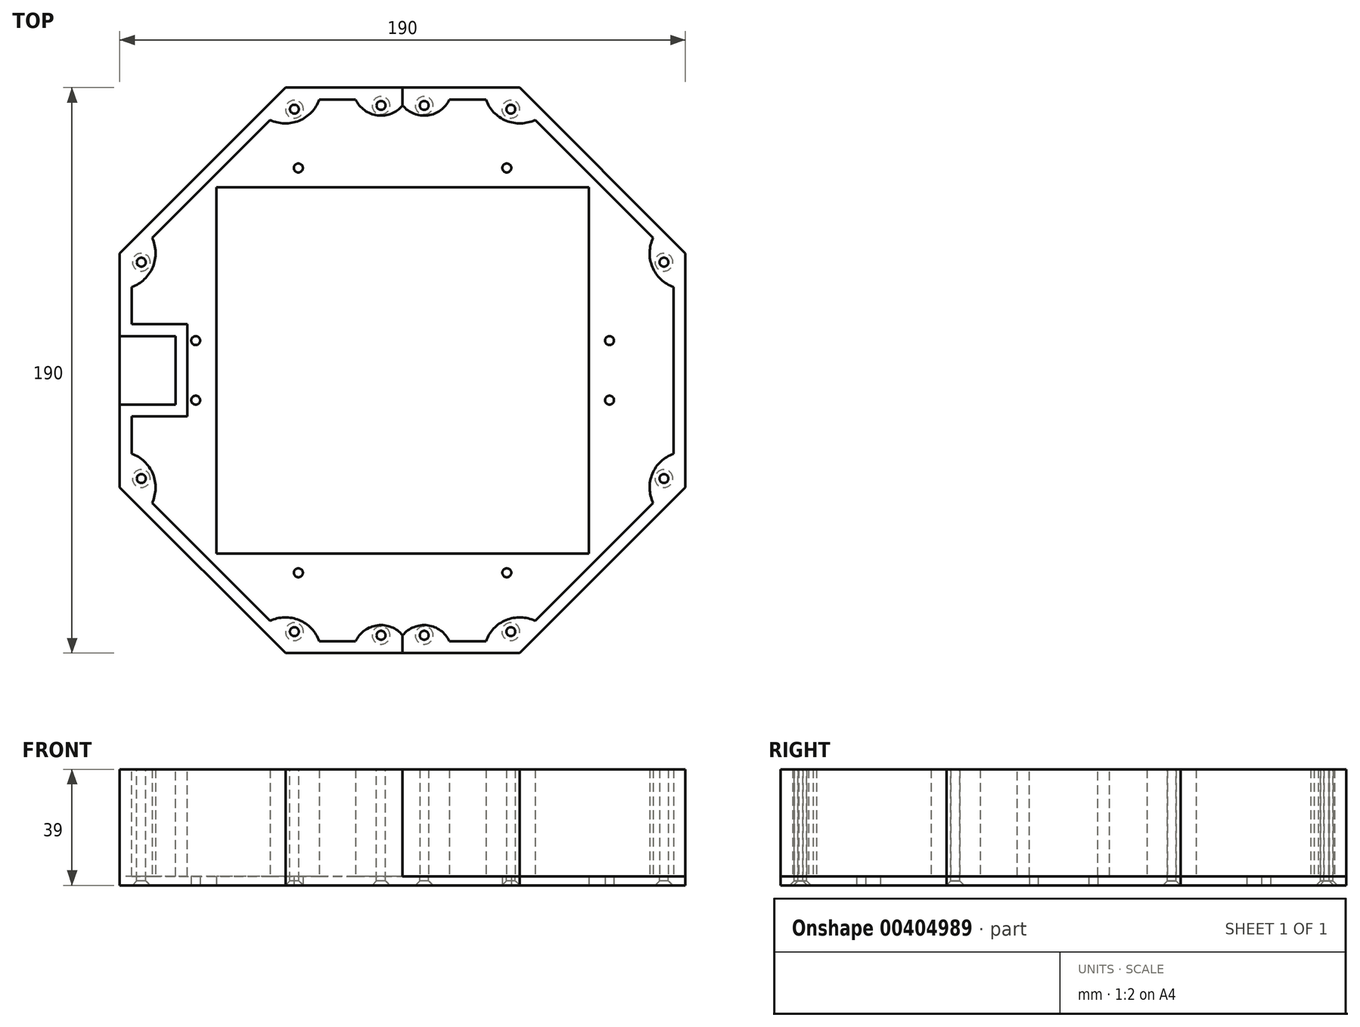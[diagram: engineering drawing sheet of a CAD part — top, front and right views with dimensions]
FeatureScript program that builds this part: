
annotation { "Feature Type Name" : "Feature", "Feature Type Description" : "" }
export const myFeature = defineFeature(function(context is Context, id is Id, definition is map)
    precondition{}
    {
        {
            var Q0;
            Q0=qCreatedBy(makeId("Top.planeOp"),FACE);
            var sketch = newSketch(context, id + "F0", { "sketchPlane" : qUnion([Q0])});
            skCircle(sketch, "E0.cCircle", {"center": v(0, 0) * mm, "radius": 95 * mm, "construction": true});
            skLineSegment(sketch, "E0.0", {"start": v(-95, -39.35) * mm, "end": v(-95, 39.35) * mm});
            skLineSegment(sketch, "E0.1", {"start": v(-95, 39.35) * mm, "end": v(-39.35, 95) * mm});
            skLineSegment(sketch, "E0.2", {"start": v(-39.35, 95) * mm, "end": v(39.35, 95) * mm});
            skLineSegment(sketch, "E0.3", {"start": v(39.35, 95) * mm, "end": v(95, 39.35) * mm});
            skLineSegment(sketch, "E0.4", {"start": v(95, 39.35) * mm, "end": v(95, -39.35) * mm});
            skLineSegment(sketch, "E0.5", {"start": v(95, -39.35) * mm, "end": v(39.35, -95) * mm});
            skLineSegment(sketch, "E0.6", {"start": v(39.35, -95) * mm, "end": v(-39.35, -95) * mm});
            skLineSegment(sketch, "E0.7", {"start": v(-39.35, -95) * mm, "end": v(-95, -39.35) * mm});
            skPoint(sketch, "E0.0.midPoint", {"position": v(-95, 0) * mm});
            skLineSegment(sketch, "E1.0", {"start": v(-91, -37.7) * mm, "end": v(-91, 37.7) * mm});
            skLineSegment(sketch, "E1.1", {"start": v(-37.7, -91) * mm, "end": v(-91, -37.7) * mm});
            skLineSegment(sketch, "E1.2", {"start": v(-91, 37.7) * mm, "end": v(-37.7, 91) * mm});
            skLineSegment(sketch, "E1.3", {"start": v(37.7, -91) * mm, "end": v(-37.7, -91) * mm});
            skLineSegment(sketch, "E1.4", {"start": v(-37.7, 91) * mm, "end": v(37.7, 91) * mm});
            skLineSegment(sketch, "E1.5", {"start": v(37.7, 91) * mm, "end": v(91, 37.7) * mm});
            skLineSegment(sketch, "E1.6", {"start": v(91, 37.7) * mm, "end": v(91, -37.7) * mm});
            skLineSegment(sketch, "E1.7", {"start": v(91, -37.7) * mm, "end": v(37.7, -91) * mm});
            skLineSegment(sketch, "E2", {"start": v(0, 91) * mm, "end": v(0, 95) * mm});
            skLineSegment(sketch, "E3", {"start": v(-95, 0) * mm, "end": v(95, 0) * mm});
            skLineSegment(sketch, "E4", {"start": v(0, -91) * mm, "end": v(0, -95) * mm});
            skCircle(sketch, "E5", {"center": v(-87.77, 36.36) * mm, "radius": 1.5 * mm});
            skCircle(sketch, "E6", {"center": v(-7.25, 89) * mm, "radius": 1.5 * mm});
            skCircle(sketch, "E7", {"center": v(7.25, 89) * mm, "radius": 1.5 * mm});
            skLineSegment(sketch, "E8", {"start": v(0, 0) * mm, "end": v(-95, 39.35) * mm, "construction": true});
            skLineSegment(sketch, "E9", {"start": v(0, 0) * mm, "end": v(0, 89) * mm, "construction": true});
            skLineSegment(sketch, "E10", {"start": v(-7.25, 89) * mm, "end": v(0, 89) * mm, "construction": true});
            skLineSegment(sketch, "E11", {"start": v(7.25, 89) * mm, "end": v(0, 89) * mm, "construction": true});
            skArc(sketch, "E12", {"start": v(-15.77, 91) * mm, "mid": v(-7.25, 85.59) * mm, "end": v(1.27, 91) * mm});
            skArc(sketch, "E13", {"start": v(-1.27, 91) * mm, "mid": v(7.25, 85.59) * mm, "end": v(15.77, 91) * mm});
            skLineSegment(sketch, "E14", {"start": v(0, 89) * mm, "end": v(0, 91) * mm});
            skArc(sketch, "E15.1.0", {"start": v(15.77, -91) * mm, "mid": v(7.25, -85.59) * mm, "end": v(-1.27, -91) * mm});
            skCircle(sketch, "E15.1.1", {"center": v(7.25, -89) * mm, "radius": 1.5 * mm});
            skArc(sketch, "E15.1.2", {"start": v(1.27, -91) * mm, "mid": v(-7.25, -85.59) * mm, "end": v(-15.77, -91) * mm});
            skCircle(sketch, "E15.1.3", {"center": v(-7.25, -89) * mm, "radius": 1.5 * mm});
            skLineSegment(sketch, "E15.1.4", {"start": v(0, -89) * mm, "end": v(0, -91) * mm});
            skArc(sketch, "E16.trimOffspring", {"start": v(-91, 28) * mm, "mid": v(-83.89, 34.75) * mm, "end": v(-84.15, 44.54) * mm});
            skCircle(sketch, "E17.1.0", {"center": v(-87.77, -36.35) * mm, "radius": 1.5 * mm});
            skArc(sketch, "E17.1.1", {"start": v(-84.15, -44.54) * mm, "mid": v(-83.89, -34.75) * mm, "end": v(-91, -28) * mm});
            skCircle(sketch, "E17.2.0", {"center": v(-36.36, -87.77) * mm, "radius": 1.5 * mm});
            skArc(sketch, "E17.2.1", {"start": v(-28, -91) * mm, "mid": v(-34.75, -83.89) * mm, "end": v(-44.54, -84.15) * mm});
            skCircle(sketch, "E17.3.0", {"center": v(36.36, -87.77) * mm, "radius": 1.5 * mm});
            skArc(sketch, "E17.3.1", {"start": v(44.54, -84.15) * mm, "mid": v(34.75, -83.89) * mm, "end": v(28, -91) * mm});
            skCircle(sketch, "E17.4.0", {"center": v(87.77, -36.36) * mm, "radius": 1.5 * mm});
            skArc(sketch, "E17.4.1", {"start": v(91, -28) * mm, "mid": v(83.89, -34.75) * mm, "end": v(84.15, -44.54) * mm});
            skCircle(sketch, "E17.5.0", {"center": v(87.77, 36.35) * mm, "radius": 1.5 * mm});
            skArc(sketch, "E17.5.1", {"start": v(84.15, 44.54) * mm, "mid": v(83.89, 34.75) * mm, "end": v(91, 28) * mm});
            skCircle(sketch, "E17.6.0", {"center": v(36.36, 87.77) * mm, "radius": 1.5 * mm});
            skArc(sketch, "E17.6.1", {"start": v(28, 91) * mm, "mid": v(34.75, 83.89) * mm, "end": v(44.54, 84.15) * mm});
            skCircle(sketch, "E17.7.0", {"center": v(-36.35, 87.77) * mm, "radius": 1.5 * mm});
            skArc(sketch, "E17.7.1", {"start": v(-44.54, 84.15) * mm, "mid": v(-34.75, 83.89) * mm, "end": v(-28, 91) * mm});
            skSolve(sketch);
        }
        {
            var Q0;
            Q0=makeQuery(id+"F0.imprint","IMPRINT",FACE,{"disambiguationData":[TD([[makeQuery(id+"F0.imprint","IMPRINT",EDGE,{"derivedFrom":sQuery(id+"F0.wireOp",EDGE,"E6")}),-1.0]])]});
            var Q1;
            Q1=makeQuery(id+"F0.imprint","IMPRINT",FACE,{"disambiguationData":[TD([[makeQuery(id+"F0.imprint","IMPRINT",EDGE,{"derivedFrom":sQuery(id+"F0.wireOp",EDGE,"E7")}),-1.0]])]});
            var Q2;
            {var subQ0=sQuery(id+"F0.wireOp",EDGE,"E14");Q2=makeQuery(id+"F0.imprint","IMPRINT",FACE,{"disambiguationData":[TD([[makeQuery(id+"F0.imprint","IMPRINT",EDGE,{"derivedFrom":subQ0}),-1.0]])]});}
            var Q3;
            {var subQ0=sQuery(id+"F0.wireOp",EDGE,"E14");Q3=makeQuery(id+"F0.imprint","IMPRINT",FACE,{"disambiguationData":[TD([[makeQuery(id+"F0.imprint","IMPRINT",EDGE,{"derivedFrom":subQ0}),1.0]])]});}
            var Q4;
            {var subQ11=sQuery(id+"F0.wireOp",EDGE,"E1.2");Q4=makeQuery(id+"F0.imprint","IMPRINT",FACE,{"disambiguationData":[TD([[makeQuery(id+"F0.imprint","IMPRINT",EDGE,{"derivedFrom":subQ11}),-1.0]])]});}
            var Q5;
            {var subQ8=sQuery(id+"F0.wireOp",EDGE,"E0.1");Q5=makeQuery(id+"F0.imprint","IMPRINT",FACE,{"disambiguationData":[TD([[makeQuery(id+"F0.imprint","IMPRINT",EDGE,{"derivedFrom":subQ8}),-1.0]])]});}
            var Q6;
            {var subQ4=sQuery(id+"F0.wireOp",EDGE,"E0.3");Q6=makeQuery(id+"F0.imprint","IMPRINT",FACE,{"disambiguationData":[TD([[makeQuery(id+"F0.imprint","IMPRINT",EDGE,{"derivedFrom":subQ4}),-1.0]])]});}
            var Q7;
            Q7=makeQuery(id+"F0.imprint","IMPRINT",FACE,{"disambiguationData":[TD([[makeQuery(id+"F0.imprint","IMPRINT",EDGE,{"derivedFrom":sQuery(id+"F0.wireOp",EDGE,"E17.5.0")}),-1.0]])]});
            var Q8;
            Q8=makeQuery(id+"F0.imprint","IMPRINT",FACE,{"disambiguationData":[TD([[makeQuery(id+"F0.imprint","IMPRINT",EDGE,{"derivedFrom":sQuery(id+"F0.wireOp",EDGE,"E17.6.0")}),-1.0]])]});
            var Q9;
            {var subQ15=sQuery(id+"F0.wireOp",EDGE,"E16.trimOffspring");Q9=makeQuery(id+"F0.imprint","IMPRINT",FACE,{"disambiguationData":[TD([[makeQuery(id+"F0.imprint","IMPRINT",EDGE,{"derivedFrom":subQ15}),-1.0]])]});}
            extrude(context, id + "F1", {"entities" : qUnion([Q0, Q1, Q2, Q3, Q4, Q5, Q6, Q7, Q8, Q9]), "oppositeDirection" : true, "depth" : 3 * mm});
        }
        {
            var Q0;
            Q0=makeQuery(id+"F0.imprint","IMPRINT",FACE,{"disambiguationData":[TD([[makeQuery(id+"F0.imprint","IMPRINT",EDGE,{"derivedFrom":sQuery(id+"F0.wireOp",EDGE,"E17.1.0")}),-1.0]])]});
            var Q1;
            Q1=makeQuery(id+"F0.imprint","IMPRINT",FACE,{"disambiguationData":[TD([[makeQuery(id+"F0.imprint","IMPRINT",EDGE,{"derivedFrom":sQuery(id+"F0.wireOp",EDGE,"E17.4.0")}),-1.0]])]});
            var Q2;
            Q2=makeQuery(id+"F0.imprint","IMPRINT",FACE,{"disambiguationData":[TD([[makeQuery(id+"F0.imprint","IMPRINT",EDGE,{"derivedFrom":sQuery(id+"F0.wireOp",EDGE,"E17.3.0")}),-1.0]])]});
            var Q3;
            Q3=makeQuery(id+"F0.imprint","IMPRINT",FACE,{"disambiguationData":[TD([[makeQuery(id+"F0.imprint","IMPRINT",EDGE,{"derivedFrom":sQuery(id+"F0.wireOp",EDGE,"E15.1.1")}),-1.0]])]});
            var Q4;
            Q4=makeQuery(id+"F0.imprint","IMPRINT",FACE,{"disambiguationData":[TD([[makeQuery(id+"F0.imprint","IMPRINT",EDGE,{"derivedFrom":sQuery(id+"F0.wireOp",EDGE,"E15.1.3")}),-1.0]])]});
            var Q5;
            Q5=makeQuery(id+"F0.imprint","IMPRINT",FACE,{"disambiguationData":[TD([[makeQuery(id+"F0.imprint","IMPRINT",EDGE,{"derivedFrom":sQuery(id+"F0.wireOp",EDGE,"E17.2.0")}),-1.0]])]});
            var Q6;
            {var subQ2=sQuery(id+"F0.wireOp",EDGE,"E15.1.4");Q6=makeQuery(id+"F0.imprint","IMPRINT",FACE,{"disambiguationData":[TD([[makeQuery(id+"F0.imprint","IMPRINT",EDGE,{"derivedFrom":subQ2}),-1.0]])]});}
            var Q7;
            {var subQ3=sQuery(id+"F0.wireOp",EDGE,"E15.1.4");Q7=makeQuery(id+"F0.imprint","IMPRINT",FACE,{"disambiguationData":[TD([[makeQuery(id+"F0.imprint","IMPRINT",EDGE,{"derivedFrom":subQ3}),1.0]])]});}
            var Q8;
            {var subQ0=sQuery(id+"F0.wireOp",EDGE,"E17.1.1");Q8=makeQuery(id+"F0.imprint","IMPRINT",FACE,{"disambiguationData":[TD([[makeQuery(id+"F0.imprint","IMPRINT",EDGE,{"derivedFrom":subQ0}),-1.0]])]});}
            var Q9;
            {var subQ16=sQuery(id+"F0.wireOp",EDGE,"E0.5");Q9=makeQuery(id+"F0.imprint","IMPRINT",FACE,{"disambiguationData":[TD([[makeQuery(id+"F0.imprint","IMPRINT",EDGE,{"derivedFrom":subQ16}),-1.0]])]});}
            var Q10;
            {var subQ9=sQuery(id+"F0.wireOp",EDGE,"E0.7");Q10=makeQuery(id+"F0.imprint","IMPRINT",FACE,{"disambiguationData":[TD([[makeQuery(id+"F0.imprint","IMPRINT",EDGE,{"derivedFrom":subQ9}),-1.0]])]});}
            extrude(context, id + "F2", {"entities" : qUnion([Q0, Q1, Q2, Q3, Q4, Q5, Q6, Q7, Q8, Q9, Q10]), "oppositeDirection" : true, "depth" : 3 * mm});
        }
        {
            var Q0;
            {var subQ16=sQuery(id+"F0.wireOp",EDGE,"E0.5");Q0=makeQuery(id+"F0.imprint","IMPRINT",FACE,{"disambiguationData":[TD([[makeQuery(id+"F0.imprint","IMPRINT",EDGE,{"derivedFrom":subQ16}),-1.0]])]});}
            var Q1;
            {var subQ9=sQuery(id+"F0.wireOp",EDGE,"E0.3");Q1=makeQuery(id+"F0.imprint","IMPRINT",FACE,{"disambiguationData":[TD([[makeQuery(id+"F0.imprint","IMPRINT",EDGE,{"derivedFrom":subQ9}),-1.0]])]});}
            var Q2;
            Q2=makeQuery(id+"F0.imprint","IMPRINT",FACE,{"disambiguationData":[TD([[makeQuery(id+"F0.imprint","IMPRINT",EDGE,{"derivedFrom":sQuery(id+"F0.wireOp",EDGE,"E7")}),-1.0]])]});
            var Q3;
            Q3=makeQuery(id+"F0.imprint","IMPRINT",FACE,{"disambiguationData":[TD([[makeQuery(id+"F0.imprint","IMPRINT",EDGE,{"derivedFrom":sQuery(id+"F0.wireOp",EDGE,"E17.6.0")}),-1.0]])]});
            var Q4;
            Q4=makeQuery(id+"F0.imprint","IMPRINT",FACE,{"disambiguationData":[TD([[makeQuery(id+"F0.imprint","IMPRINT",EDGE,{"derivedFrom":sQuery(id+"F0.wireOp",EDGE,"E17.5.0")}),-1.0]])]});
            var Q5;
            Q5=makeQuery(id+"F0.imprint","IMPRINT",FACE,{"disambiguationData":[TD([[makeQuery(id+"F0.imprint","IMPRINT",EDGE,{"derivedFrom":sQuery(id+"F0.wireOp",EDGE,"E17.4.0")}),-1.0]])]});
            var Q6;
            Q6=makeQuery(id+"F0.imprint","IMPRINT",FACE,{"disambiguationData":[TD([[makeQuery(id+"F0.imprint","IMPRINT",EDGE,{"derivedFrom":sQuery(id+"F0.wireOp",EDGE,"E17.3.0")}),-1.0]])]});
            var Q7;
            Q7=makeQuery(id+"F0.imprint","IMPRINT",FACE,{"disambiguationData":[TD([[makeQuery(id+"F0.imprint","IMPRINT",EDGE,{"derivedFrom":sQuery(id+"F0.wireOp",EDGE,"E15.1.1")}),-1.0]])]});
            var Q8;
            {var subQ0=sQuery(id+"F0.wireOp",EDGE,"E14");Q8=makeQuery(id+"F0.imprint","IMPRINT",FACE,{"disambiguationData":[TD([[makeQuery(id+"F0.imprint","IMPRINT",EDGE,{"derivedFrom":subQ0}),-1.0]])]});}
            var Q9;
            {var subQ3=sQuery(id+"F0.wireOp",EDGE,"E15.1.4");Q9=makeQuery(id+"F0.imprint","IMPRINT",FACE,{"disambiguationData":[TD([[makeQuery(id+"F0.imprint","IMPRINT",EDGE,{"derivedFrom":subQ3}),1.0]])]});}
            extrude(context, id + "F3", {"entities" : qUnion([Q0, Q1, Q2, Q3, Q4, Q5, Q6, Q7, Q8, Q9]), "depth" : 36 * mm});
        }
        {
            var Q0;
            {var subQ2=sQuery(id+"F0.wireOp",EDGE,"E15.1.4");Q0=makeQuery(id+"F0.imprint","IMPRINT",FACE,{"disambiguationData":[TD([[makeQuery(id+"F0.imprint","IMPRINT",EDGE,{"derivedFrom":subQ2}),-1.0]])]});}
            var Q1;
            Q1=makeQuery(id+"F0.imprint","IMPRINT",FACE,{"disambiguationData":[TD([[makeQuery(id+"F0.imprint","IMPRINT",EDGE,{"derivedFrom":sQuery(id+"F0.wireOp",EDGE,"E15.1.3")}),-1.0]])]});
            var Q2;
            Q2=makeQuery(id+"F0.imprint","IMPRINT",FACE,{"disambiguationData":[TD([[makeQuery(id+"F0.imprint","IMPRINT",EDGE,{"derivedFrom":sQuery(id+"F0.wireOp",EDGE,"E17.2.0")}),-1.0]])]});
            var Q3;
            {var subQ9=sQuery(id+"F0.wireOp",EDGE,"E0.7");Q3=makeQuery(id+"F0.imprint","IMPRINT",FACE,{"disambiguationData":[TD([[makeQuery(id+"F0.imprint","IMPRINT",EDGE,{"derivedFrom":subQ9}),-1.0]])]});}
            var Q4;
            Q4=makeQuery(id+"F0.imprint","IMPRINT",FACE,{"disambiguationData":[TD([[makeQuery(id+"F0.imprint","IMPRINT",EDGE,{"derivedFrom":sQuery(id+"F0.wireOp",EDGE,"E17.1.0")}),-1.0]])]});
            var Q5;
            {var subQ14=sQuery(id+"F0.wireOp",EDGE,"E0.1");Q5=makeQuery(id+"F0.imprint","IMPRINT",FACE,{"disambiguationData":[TD([[makeQuery(id+"F0.imprint","IMPRINT",EDGE,{"derivedFrom":subQ14}),-1.0]])]});}
            var Q6;
            Q6=makeQuery(id+"F0.imprint","IMPRINT",FACE,{"disambiguationData":[TD([[makeQuery(id+"F0.imprint","IMPRINT",EDGE,{"derivedFrom":sQuery(id+"F0.wireOp",EDGE,"E5")}),-1.0]])]});
            var Q7;
            Q7=makeQuery(id+"F0.imprint","IMPRINT",FACE,{"disambiguationData":[TD([[makeQuery(id+"F0.imprint","IMPRINT",EDGE,{"derivedFrom":sQuery(id+"F0.wireOp",EDGE,"E17.7.0")}),-1.0]])]});
            var Q8;
            Q8=makeQuery(id+"F0.imprint","IMPRINT",FACE,{"disambiguationData":[TD([[makeQuery(id+"F0.imprint","IMPRINT",EDGE,{"derivedFrom":sQuery(id+"F0.wireOp",EDGE,"E6")}),-1.0]])]});
            var Q9;
            {var subQ0=sQuery(id+"F0.wireOp",EDGE,"E14");Q9=makeQuery(id+"F0.imprint","IMPRINT",FACE,{"disambiguationData":[TD([[makeQuery(id+"F0.imprint","IMPRINT",EDGE,{"derivedFrom":subQ0}),1.0]])]});}
            extrude(context, id + "F4", {"entities" : qUnion([Q0, Q1, Q2, Q3, Q4, Q5, Q6, Q7, Q8, Q9]), "depth" : 36 * mm});
        }
        {
            var Q0;
            Q0=makeQuery(id+"F2.opExtrude","CAP_FACE",FACE,{"disambiguationData":[OSD([sQuery(id+"F0.wireOp",EDGE,"E0.0"),sQuery(id+"F0.wireOp",EDGE,"E0.1"),sQuery(id+"F0.wireOp",EDGE,"E0.2"),sQuery(id+"F0.wireOp",EDGE,"E0.3"),sQuery(id+"F0.wireOp",EDGE,"E0.4"),sQuery(id+"F0.wireOp",EDGE,"E3")])],"isStart":false});
            var sketch = newSketch(context, id + "F5", { "sketchPlane" : qUnion([Q0])});
            skLineSegment(sketch, "E18", {"start": v(0, 0) * mm, "end": v(-74, 0) * mm, "construction": true});
            skLineSegment(sketch, "E19", {"start": v(0, 0) * mm, "end": v(74, 0) * mm, "construction": true});
            skLineSegment(sketch, "E20.bottom", {"start": v(35, 68) * mm, "end": v(-35, 68) * mm, "construction": true});
            skLineSegment(sketch, "E20.top", {"start": v(35, -68) * mm, "end": v(-35, -68) * mm, "construction": true});
            skLineSegment(sketch, "E20.left", {"start": v(35, 68) * mm, "end": v(35, -68) * mm, "construction": true});
            skLineSegment(sketch, "E20.right", {"start": v(-35, 68) * mm, "end": v(-35, -68) * mm, "construction": true});
            skPoint(sketch, "E20.middle", {"position": v(0, 0) * mm});
            skCircle(sketch, "E21", {"center": v(-35, 68) * mm, "radius": 1.5 * mm});
            skCircle(sketch, "E22", {"center": v(35, 68) * mm, "radius": 1.5 * mm});
            skCircle(sketch, "E23", {"center": v(35, -68) * mm, "radius": 1.5 * mm});
            skCircle(sketch, "E24", {"center": v(-35, -68) * mm, "radius": 1.5 * mm});
            skLineSegment(sketch, "E25.bottom", {"start": v(-62.5, 61.5) * mm, "end": v(62.5, 61.5) * mm});
            skLineSegment(sketch, "E25.top", {"start": v(-62.5, -61.5) * mm, "end": v(62.5, -61.5) * mm});
            skLineSegment(sketch, "E25.left", {"start": v(-62.5, 61.5) * mm, "end": v(-62.5, -61.5) * mm});
            skLineSegment(sketch, "E25.right", {"start": v(62.5, 61.5) * mm, "end": v(62.5, -61.5) * mm});
            skLineSegment(sketch, "E26", {"start": v(-69.5, 0) * mm, "end": v(-69.5, -10) * mm});
            skLineSegment(sketch, "E27", {"start": v(-69.5, 0) * mm, "end": v(-69.5, 10) * mm});
            skCircle(sketch, "E28", {"center": v(-69.5, -10) * mm, "radius": 1.5 * mm});
            skCircle(sketch, "E29", {"center": v(-69.5, 10) * mm, "radius": 1.5 * mm});
            skLineSegment(sketch, "E30", {"start": v(0, 0) * mm, "end": v(0, -18.95) * mm, "construction": true});
            skCircle(sketch, "E31.MirrorC", {"center": v(69.5, 10) * mm, "radius": 1.5 * mm});
            skCircle(sketch, "E32.MirrorC", {"center": v(69.5, -10) * mm, "radius": 1.5 * mm});
            skSolve(sketch);
        }
        {
            var Q0;
            Q0=qSketchRegion(id+"F5",true);
            extrude(context, id + "F6", {"entities" : qUnion([Q0]), "operationType" : NewBodyOperationType.REMOVE, "oppositeDirection" : true, "depth" : 25 * mm});
        }
        {
            var Q0;
            Q0=makeQuery(id+"F4.opExtrude","CAP_FACE",FACE,{"disambiguationData":[OSD([sQuery(id+"F0.wireOp",EDGE,"E0.0"),sQuery(id+"F0.wireOp",EDGE,"E0.1"),sQuery(id+"F0.wireOp",EDGE,"E0.2"),sQuery(id+"F0.wireOp",EDGE,"E0.6"),sQuery(id+"F0.wireOp",EDGE,"E0.7"),sQuery(id+"F0.wireOp",EDGE,"E1.0"),sQuery(id+"F0.wireOp",EDGE,"E1.1"),sQuery(id+"F0.wireOp",EDGE,"E1.2"),sQuery(id+"F0.wireOp",EDGE,"E1.3"),sQuery(id+"F0.wireOp",EDGE,"E1.4"),sQuery(id+"F0.wireOp",EDGE,"E2"),sQuery(id+"F0.wireOp",EDGE,"E4"),sQuery(id+"F0.wireOp",EDGE,"E5"),sQuery(id+"F0.wireOp",EDGE,"E6"),sQuery(id+"F0.wireOp",EDGE,"E12"),sQuery(id+"F0.wireOp",EDGE,"E14"),sQuery(id+"F0.wireOp",EDGE,"E15.1.2"),sQuery(id+"F0.wireOp",EDGE,"E15.1.3"),sQuery(id+"F0.wireOp",EDGE,"E15.1.4"),sQuery(id+"F0.wireOp",EDGE,"E16.trimOffspring"),sQuery(id+"F0.wireOp",EDGE,"E17.1.0"),sQuery(id+"F0.wireOp",EDGE,"E17.1.1"),sQuery(id+"F0.wireOp",EDGE,"E17.2.0"),sQuery(id+"F0.wireOp",EDGE,"E17.2.1"),sQuery(id+"F0.wireOp",EDGE,"E17.7.0"),sQuery(id+"F0.wireOp",EDGE,"E17.7.1")])],"isStart":false});
            var sketch = newSketch(context, id + "F7", { "sketchPlane" : qUnion([Q0])});
            skLineSegment(sketch, "E33.bottom", {"start": v(-95, -11.5) * mm, "end": v(-76.26, -11.5) * mm});
            skLineSegment(sketch, "E33.top", {"start": v(-95, 11.5) * mm, "end": v(-76.26, 11.5) * mm});
            skLineSegment(sketch, "E33.left", {"start": v(-95, -11.5) * mm, "end": v(-95, 11.5) * mm});
            skLineSegment(sketch, "E33.right", {"start": v(-76.26, -11.5) * mm, "end": v(-76.26, 11.5) * mm});
            skLineSegment(sketch, "E34.bottom", {"start": v(-95, -15.5) * mm, "end": v(-72.26, -15.5) * mm});
            skLineSegment(sketch, "E34.top", {"start": v(-95, 15.5) * mm, "end": v(-72.26, 15.5) * mm});
            skLineSegment(sketch, "E34.left", {"start": v(-95, -15.5) * mm, "end": v(-95, 15.5) * mm});
            skLineSegment(sketch, "E34.right", {"start": v(-72.26, -15.5) * mm, "end": v(-72.26, 15.5) * mm});
            skPoint(sketch, "E35", {"position": v(-95, 0) * mm});
            skSolve(sketch);
        }
        {
            var Q0;
            {var subQ0=sQuery(id+"F7.wireOp",EDGE,"E34.left");var subQ1=sQuery(id+"F7.wireOp",EDGE,"E33.bottom");var subQ2=makeQuery(id+"F7.imprint","INTERSECT",VERTEX,{"derivedFrom":[subQ1,subQ0]});Q0=makeQuery(id+"F7.imprint","IMPRINT",FACE,{"disambiguationData":[TD([[makeQuery(id+"F7.imprint","IMPRINT",EDGE,{"disambiguationData":[TD([[subQ2,-1.0]])],"derivedFrom":subQ1}),1.0]])]});}
            extrude(context, id + "F8", {"entities" : qUnion([Q0]), "operationType" : NewBodyOperationType.REMOVE, "endBound" : BoundingType.UP_TO_NEXT, "oppositeDirection" : true, "depth" : 25 * mm});
        }
        {
            var Q0;
            {var subQ0=sQuery(id+"F7.wireOp",EDGE,"E33.right");Q0=makeQuery(id+"F7.imprint","IMPRINT",FACE,{"disambiguationData":[TD([[makeQuery(id+"F7.imprint","IMPRINT",EDGE,{"derivedFrom":subQ0}),-1.0]])]});}
            var Q1;
            Q1=makeQuery(id+"F2.opExtrude","CAP_FACE",FACE,{"disambiguationData":[OSD([sQuery(id+"F0.wireOp",EDGE,"E0.0"),sQuery(id+"F0.wireOp",EDGE,"E0.4"),sQuery(id+"F0.wireOp",EDGE,"E0.5"),sQuery(id+"F0.wireOp",EDGE,"E0.6"),sQuery(id+"F0.wireOp",EDGE,"E0.7"),sQuery(id+"F0.wireOp",EDGE,"E3"),sQuery(id+"F0.wireOp",EDGE,"E15.1.1"),sQuery(id+"F0.wireOp",EDGE,"E15.1.3"),sQuery(id+"F0.wireOp",EDGE,"E17.1.0"),sQuery(id+"F0.wireOp",EDGE,"E17.2.0"),sQuery(id+"F0.wireOp",EDGE,"E17.3.0"),sQuery(id+"F0.wireOp",EDGE,"E17.4.0")])],"isStart":true});
            extrude(context, id + "F9", {"entities" : qUnion([Q0]), "operationType" : NewBodyOperationType.ADD, "endBound" : BoundingType.UP_TO_SURFACE, "oppositeDirection" : true, "endBoundEntityFace" : qUnion([Q1]), "depth" : 25 * mm});
        }
        {
            var Q0;
            Q0=makeQuery(id+"F2.opExtrude","CAP_EDGE",EDGE,{"disambiguationData":[OSD([sQuery(id+"F0.wireOp",EDGE,"E17.2.0")])],"isStart":false});
            var Q1;
            Q1=makeQuery(id+"F2.opExtrude","CAP_EDGE",EDGE,{"disambiguationData":[OSD([sQuery(id+"F0.wireOp",EDGE,"E15.1.3")])],"isStart":false});
            var Q2;
            Q2=makeQuery(id+"F2.opExtrude","CAP_EDGE",EDGE,{"disambiguationData":[OSD([sQuery(id+"F0.wireOp",EDGE,"E15.1.1")])],"isStart":false});
            var Q3;
            Q3=makeQuery(id+"F2.opExtrude","CAP_EDGE",EDGE,{"disambiguationData":[OSD([sQuery(id+"F0.wireOp",EDGE,"E17.3.0")])],"isStart":false});
            var Q4;
            Q4=makeQuery(id+"F6.boolean.opBoolean","COPY",EDGE,{"derivedFrom":makeQuery(id+"F6.opExtrude","CAP_EDGE",EDGE,{"disambiguationData":[OSD([sQuery(id+"F5.wireOp",EDGE,"E22")])],"isStart":true})});
            var Q5;
            Q5=makeQuery(id+"F6.boolean.opBoolean","COPY",EDGE,{"derivedFrom":makeQuery(id+"F6.opExtrude","CAP_EDGE",EDGE,{"disambiguationData":[OSD([sQuery(id+"F5.wireOp",EDGE,"E21")])],"isStart":true})});
            var Q6;
            Q6=makeQuery(id+"F2.opExtrude","CAP_EDGE",EDGE,{"disambiguationData":[OSD([sQuery(id+"F0.wireOp",EDGE,"E17.1.0")])],"isStart":false});
            var Q7;
            Q7=makeQuery(id+"F2.opExtrude","CAP_EDGE",EDGE,{"disambiguationData":[OSD([sQuery(id+"F0.wireOp",EDGE,"E17.4.0")])],"isStart":false});
            var Q8;
            Q8=makeQuery(id+"F1.opExtrude","CAP_EDGE",EDGE,{"disambiguationData":[OSD([sQuery(id+"F0.wireOp",EDGE,"E17.5.0")])],"isStart":false});
            var Q9;
            Q9=makeQuery(id+"F6.boolean.opBoolean","COPY",EDGE,{"derivedFrom":makeQuery(id+"F6.opExtrude","CAP_EDGE",EDGE,{"disambiguationData":[OSD([sQuery(id+"F5.wireOp",EDGE,"E23")])],"isStart":true})});
            var Q10;
            Q10=makeQuery(id+"F1.opExtrude","CAP_EDGE",EDGE,{"disambiguationData":[OSD([sQuery(id+"F0.wireOp",EDGE,"E17.6.0")])],"isStart":false});
            var Q11;
            Q11=makeQuery(id+"F1.opExtrude","CAP_EDGE",EDGE,{"disambiguationData":[OSD([sQuery(id+"F0.wireOp",EDGE,"E7")])],"isStart":false});
            var Q12;
            Q12=makeQuery(id+"F1.opExtrude","CAP_EDGE",EDGE,{"disambiguationData":[OSD([sQuery(id+"F0.wireOp",EDGE,"E6")])],"isStart":false});
            var Q13;
            Q13=makeQuery(id+"F6.boolean.opBoolean","COPY",EDGE,{"derivedFrom":makeQuery(id+"F6.opExtrude","CAP_EDGE",EDGE,{"disambiguationData":[OSD([sQuery(id+"F5.wireOp",EDGE,"E24")])],"isStart":true})});
            var Q14;
            Q14=makeQuery(id+"F1.opExtrude","CAP_EDGE",EDGE,{"disambiguationData":[OSD([sQuery(id+"F0.wireOp",EDGE,"E17.7.0")])],"isStart":false});
            var Q15;
            Q15=makeQuery(id+"F1.opExtrude","CAP_EDGE",EDGE,{"disambiguationData":[OSD([sQuery(id+"F0.wireOp",EDGE,"E5")])],"isStart":false});
            var Q16;
            Q16=makeQuery(id+"F6.boolean.opBoolean","COPY",EDGE,{"derivedFrom":makeQuery(id+"F6.opExtrude","CAP_EDGE",EDGE,{"disambiguationData":[OSD([sQuery(id+"F5.wireOp",EDGE,"E29")])],"isStart":true})});
            var Q17;
            Q17=makeQuery(id+"F6.boolean.opBoolean","COPY",EDGE,{"derivedFrom":makeQuery(id+"F6.opExtrude","CAP_EDGE",EDGE,{"disambiguationData":[OSD([sQuery(id+"F5.wireOp",EDGE,"E28")])],"isStart":true})});
            var Q18;
            Q18=makeQuery(id+"F6.boolean.opBoolean","COPY",EDGE,{"derivedFrom":makeQuery(id+"F6.opExtrude","CAP_EDGE",EDGE,{"disambiguationData":[OSD([sQuery(id+"F5.wireOp",EDGE,"E32.MirrorC")])],"isStart":true})});
            var Q19;
            Q19=makeQuery(id+"F6.boolean.opBoolean","COPY",EDGE,{"derivedFrom":makeQuery(id+"F6.opExtrude","CAP_EDGE",EDGE,{"disambiguationData":[OSD([sQuery(id+"F5.wireOp",EDGE,"E31.MirrorC")])],"isStart":true})});
            chamfer(context, id + "F10", {"entities" : qUnion([Q0, Q1, Q2, Q3, Q4, Q5, Q6, Q7, Q8, Q9, Q10, Q11, Q12, Q13, Q14, Q15, Q16, Q17, Q18, Q19]), "width" : 1.5 * mm, "tangentPropagation" : true});
        }
    });
